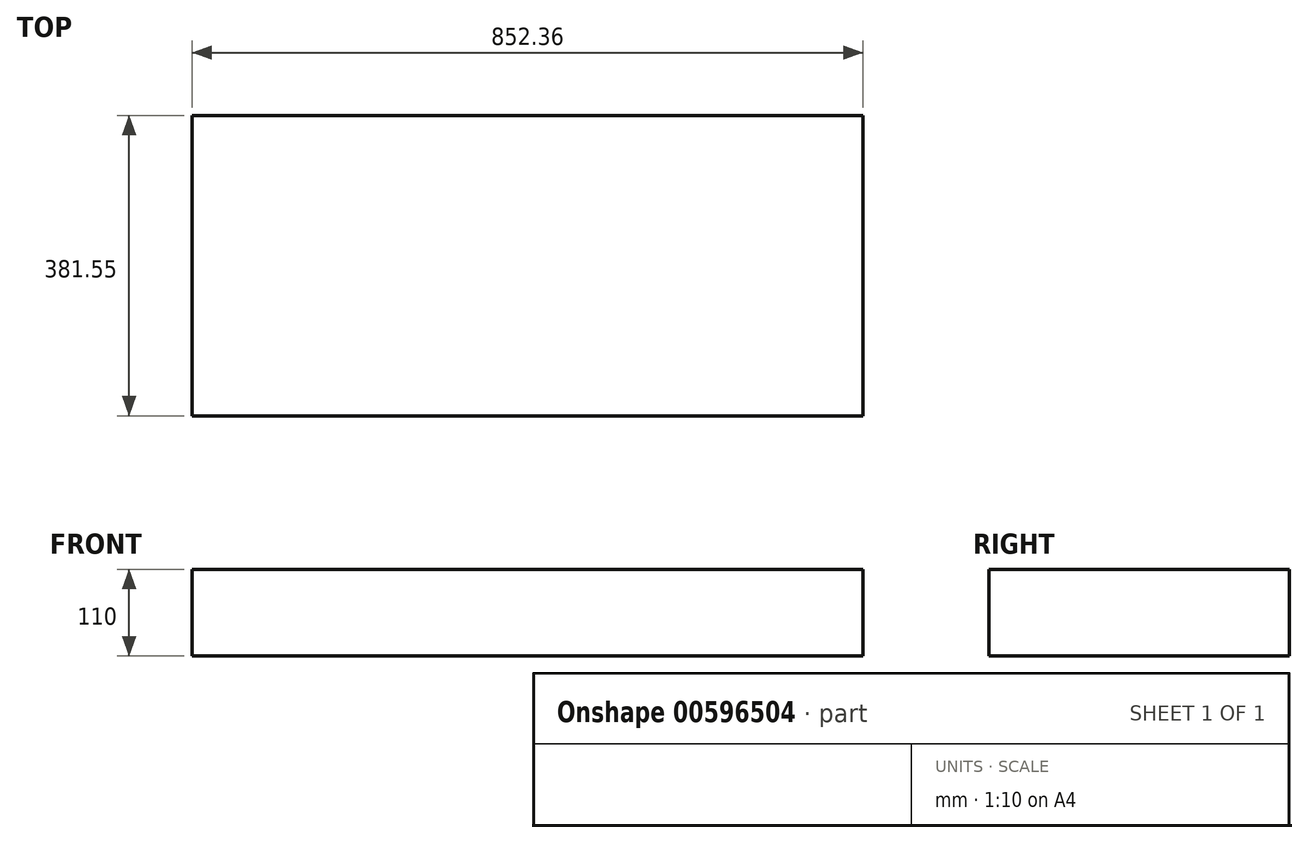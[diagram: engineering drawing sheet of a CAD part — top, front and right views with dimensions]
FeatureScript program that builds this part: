
annotation { "Feature Type Name" : "Feature", "Feature Type Description" : "" }
export const myFeature = defineFeature(function(context is Context, id is Id, definition is map)
    precondition{}
    {
        {
            var Q0;
            Q0=qCreatedBy(makeId("Top.planeOp"),FACE);
            var sketch = newSketch(context, id + "F0", { "sketchPlane" : qUnion([Q0])});
            skLineSegment(sketch, "E0.bottom", {"start": v(-438.44, 149.8) * mm, "end": v(413.92, 149.8) * mm});
            skLineSegment(sketch, "E0.top", {"start": v(-438.44, -231.74) * mm, "end": v(413.92, -231.74) * mm});
            skLineSegment(sketch, "E0.left", {"start": v(-438.44, 149.8) * mm, "end": v(-438.44, -231.74) * mm});
            skLineSegment(sketch, "E0.right", {"start": v(413.92, 149.8) * mm, "end": v(413.92, -231.74) * mm});
            skSolve(sketch);
        }
        {
            var Q0;
            Q0=makeQuery(id+"F0.imprint","IMPRINT",FACE,{"disambiguationData":[TD([[makeQuery(id+"F0.imprint","IMPRINT",EDGE,{"derivedFrom":sQuery(id+"F0.wireOp",EDGE,"E0.bottom")}),-1.0]])]});
            extrude(context, id + "F1", {"entities" : qUnion([Q0]), "depth" : 110 * mm, "offsetDistance" : 25 * mm});
        }
    });
